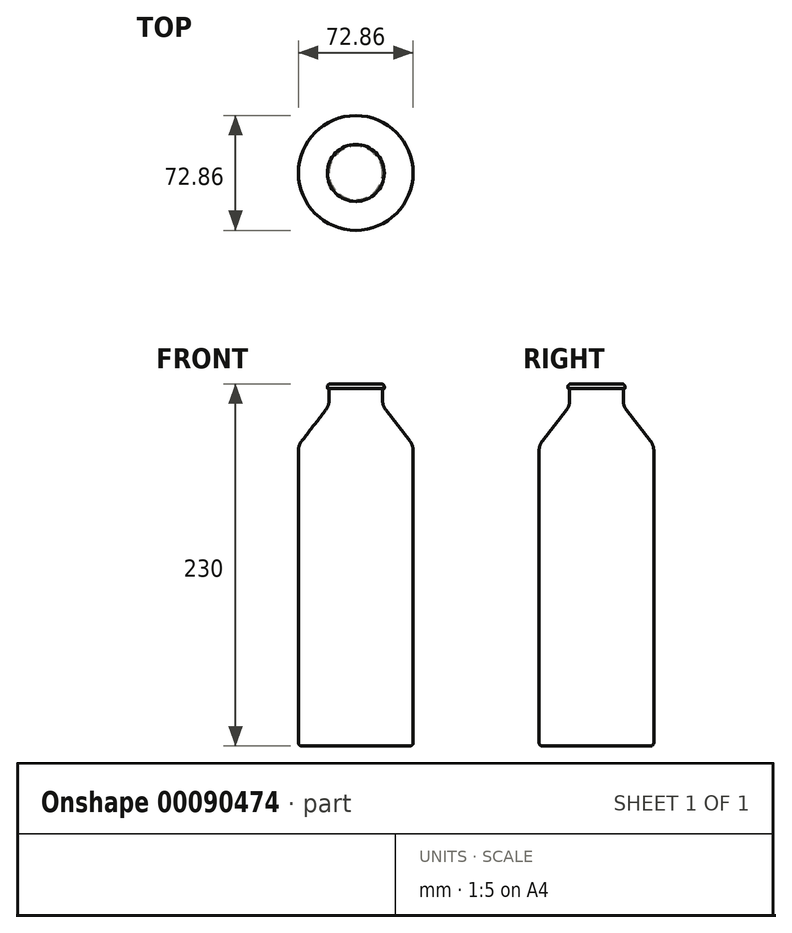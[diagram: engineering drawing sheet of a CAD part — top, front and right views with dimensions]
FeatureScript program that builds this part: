
annotation { "Feature Type Name" : "Feature", "Feature Type Description" : "" }
export const myFeature = defineFeature(function(context is Context, id is Id, definition is map)
    precondition{}
    {
        {
            var Q0;
            Q0=qCreatedBy(makeId("Front.planeOp"),FACE);
            var sketch = newSketch(context, id + "F0", { "sketchPlane" : qUnion([Q0])});
            skLineSegment(sketch, "E0", {"start": v(0, 0) * mm, "end": v(0, 230) * mm});
            skLineSegment(sketch, "E1", {"start": v(36.42, 187.57) * mm, "end": v(36.43, 2) * mm});
            skLineSegment(sketch, "E2", {"start": v(34.43, 0) * mm, "end": v(0, 0) * mm});
            skLineSegment(sketch, "E3", {"start": v(17.85, 227) * mm, "end": v(17.25, 227) * mm});
            skLineSegment(sketch, "E4", {"start": v(17, 226.75) * mm, "end": v(17, 219.43) * mm});
            skLineSegment(sketch, "E5", {"start": v(19.1, 213.3) * mm, "end": v(34.32, 193.7) * mm});
            skPoint(sketch, "E6.visualSharp", {"position": v(36.43, 0) * mm});
            skArc(sketch, "E6.filletArc", {"start": v(34.43, 0) * mm, "mid": v(35.84, 0.59) * mm, "end": v(36.43, 2) * mm});
            skPoint(sketch, "E7.visualSharp", {"position": v(36.42, 191) * mm});
            skArc(sketch, "E7.filletArc", {"start": v(36.42, 187.57) * mm, "mid": v(35.88, 190.81) * mm, "end": v(34.32, 193.7) * mm});
            skPoint(sketch, "E8.visualSharp", {"position": v(18.1, 230) * mm});
            skPoint(sketch, "E9.visualSharp", {"position": v(17, 216) * mm});
            skArc(sketch, "E9.filletArc", {"start": v(17, 219.43) * mm, "mid": v(17.54, 216.19) * mm, "end": v(19.1, 213.3) * mm});
            skLineSegment(sketch, "E10", {"start": v(18.1, 229.75) * mm, "end": v(18.1, 227.25) * mm});
            skLineSegment(sketch, "E11", {"start": v(17.85, 230) * mm, "end": v(0, 230) * mm});
            skPoint(sketch, "E12.visualSharp", {"position": v(18.1, 227) * mm});
            skArc(sketch, "E12.filletArc", {"start": v(17.85, 227) * mm, "mid": v(18.03, 227.07) * mm, "end": v(18.1, 227.25) * mm});
            skLineSegment(sketch, "E13", {"start": v(16.1, 230) * mm, "end": v(17.85, 230) * mm});
            skLineSegment(sketch, "E14", {"start": v(18.1, 228) * mm, "end": v(18.1, 229.75) * mm});
            skArc(sketch, "E15.filletArc", {"start": v(18.1, 228) * mm, "mid": v(17.51, 229.41) * mm, "end": v(16.1, 230) * mm});
            skPoint(sketch, "E16.visualSharp", {"position": v(17, 227) * mm});
            skArc(sketch, "E16.filletArc", {"start": v(17.25, 227) * mm, "mid": v(17.07, 226.93) * mm, "end": v(17, 226.75) * mm});
            skSolve(sketch);
        }
        {
            var Q0;
            Q0=makeQuery(id+"F0.imprint","IMPRINT",FACE,{"disambiguationData":[TD([[makeQuery(id+"F0.imprint","IMPRINT",EDGE,{"derivedFrom":sQuery(id+"F0.wireOp",EDGE,"E0")}),-1.0]])]});
            var Q1;
            Q1=sQuery(id+"F0.wireOp",EDGE,"E0");
            revolve(context, id + "F1", {"entities" : qUnion([Q0]), "axis" : qUnion([Q1]), "revolveType" : RevolveType.FULL});
        }
    });
